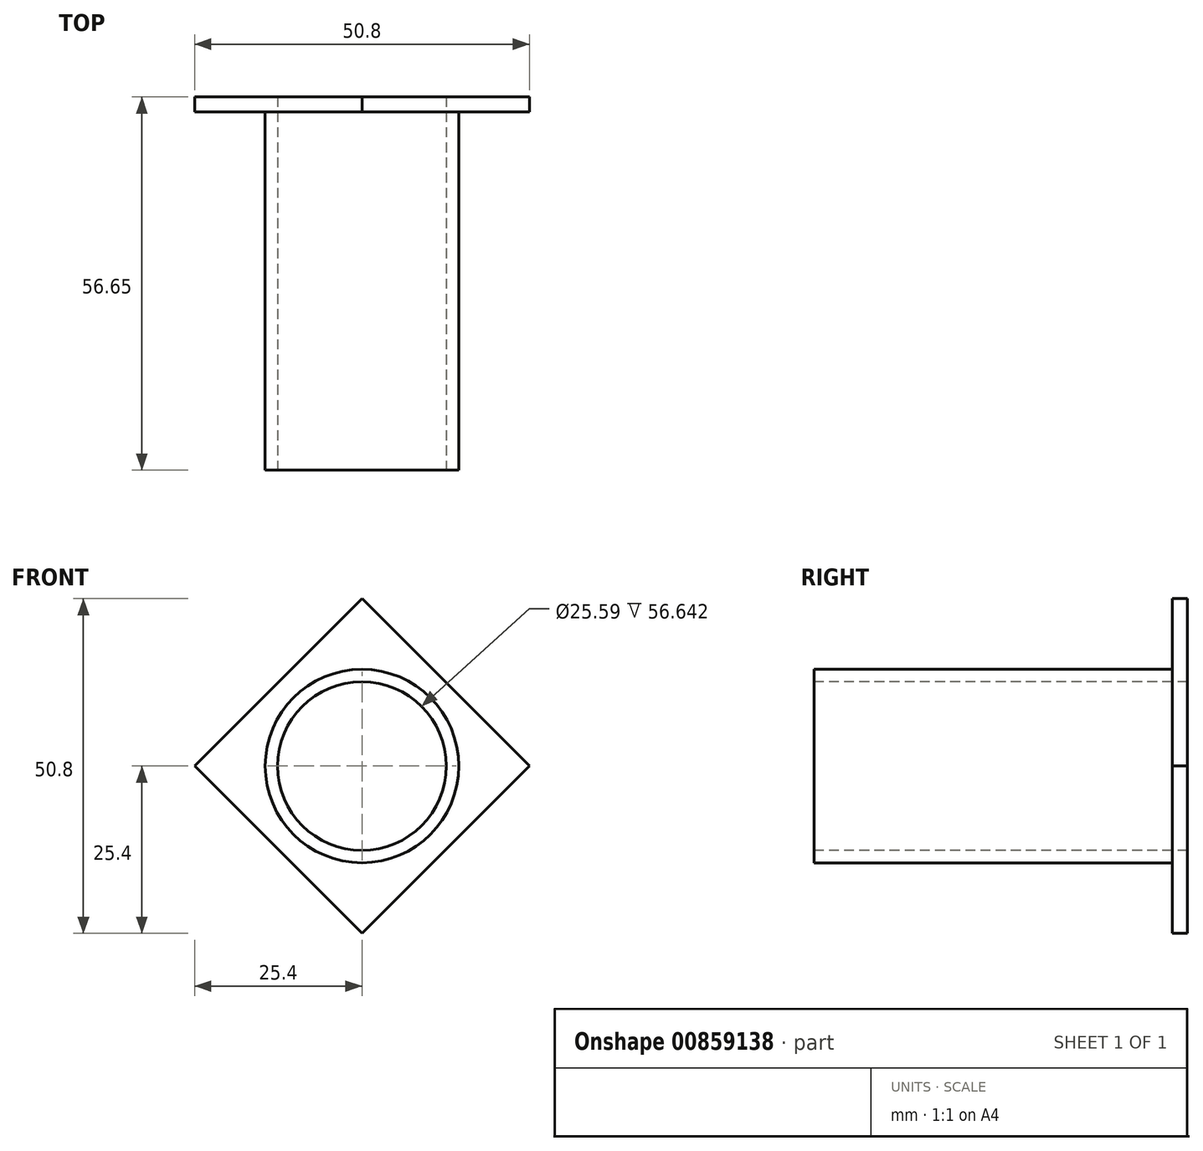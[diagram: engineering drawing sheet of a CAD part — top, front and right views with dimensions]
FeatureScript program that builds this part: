
annotation { "Feature Type Name" : "Feature", "Feature Type Description" : "" }
export const myFeature = defineFeature(function(context is Context, id is Id, definition is map)
    precondition{}
    {
        {
            var Q0;
            Q0=qCreatedBy(makeId("Front.planeOp"),FACE);
            var sketch = newSketch(context, id + "F0", { "sketchPlane" : qUnion([Q0])});
            skLineSegment(sketch, "E0", {"start": v(-25.4, 0) * mm, "end": v(0, 25.4) * mm});
            skLineSegment(sketch, "E1", {"start": v(0, 25.4) * mm, "end": v(25.4, 0) * mm});
            skLineSegment(sketch, "E2", {"start": v(25.4, 0) * mm, "end": v(0, -25.4) * mm});
            skLineSegment(sketch, "E3", {"start": v(0, -25.4) * mm, "end": v(-25.4, 0) * mm});
            skSolve(sketch);
        }
        {
            var Q0;
            Q0=qCreatedBy(makeId("Front.planeOp"),FACE);
            var sketch = newSketch(context, id + "F1", { "sketchPlane" : qUnion([Q0])});
            skCircle(sketch, "E4", {"center": v(0, 0) * mm, "radius": 14.68 * mm});
            skSolve(sketch);
        }
        {
            var Q0;
            Q0=makeQuery(id+"F0.imprint","IMPRINT",FACE,{"disambiguationData":[TD([[makeQuery(id+"F0.imprint","IMPRINT",EDGE,{"derivedFrom":sQuery(id+"F0.wireOp",EDGE,"E0")}),-1.0]])]});
            extrude(context, id + "F2", {"entities" : qUnion([Q0]), "oppositeDirection" : true, "depth" : 2.3 * mm, "offsetDistance" : 25.4 * mm});
        }
        {
            var Q0;
            Q0=qSketchRegion(id+"F1",true);
            extrude(context, id + "F3", {"entities" : qUnion([Q0]), "operationType" : NewBodyOperationType.ADD, "depth" : 54.36 * mm, "offsetDistance" : 25.4 * mm});
        }
        {
            var Q0;
            Q0=makeQuery(id+"F3.opExtrude","CAP_FACE",FACE,{"disambiguationData":[OSD([sQuery(id+"F1.wireOp",EDGE,"E4")])],"isStart":false});
            var sketch = newSketch(context, id + "F4", { "sketchPlane" : qUnion([Q0])});
            skCircle(sketch, "E5", {"center": v(0, 0) * mm, "radius": 12.8 * mm});
            skSolve(sketch);
        }
        {
            var Q0;
            Q0=qSketchRegion(id+"F4",true);
            extrude(context, id + "F5", {"entities" : qUnion([Q0]), "operationType" : NewBodyOperationType.REMOVE, "oppositeDirection" : true, "depth" : 76.2 * mm, "offsetDistance" : 25.4 * mm});
        }
    });
